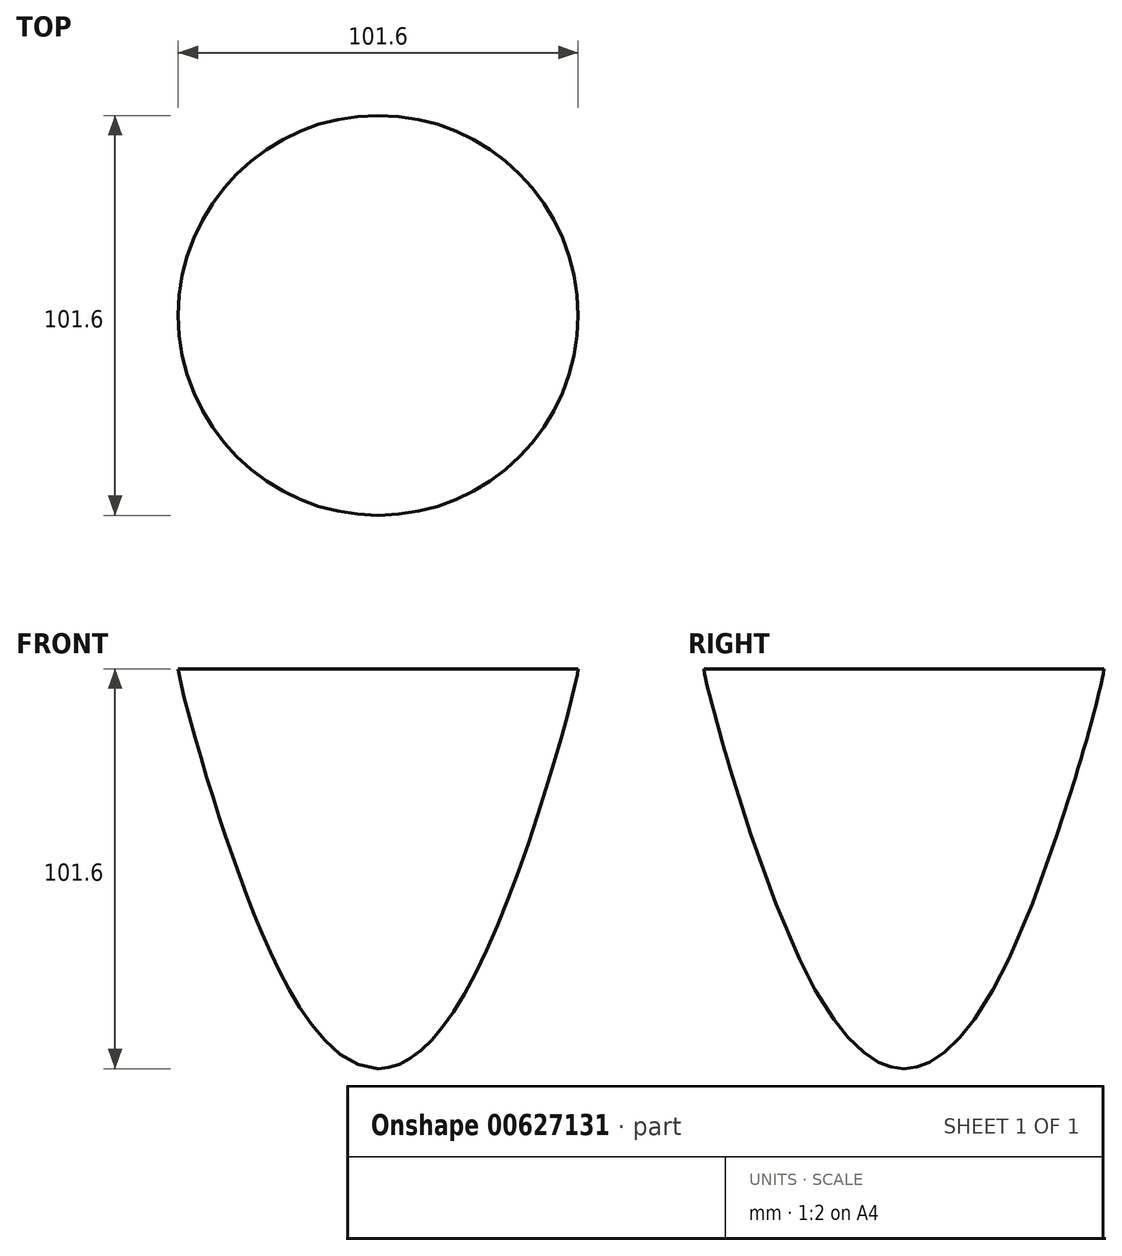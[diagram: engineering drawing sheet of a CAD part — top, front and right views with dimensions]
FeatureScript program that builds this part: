
annotation { "Feature Type Name" : "Feature", "Feature Type Description" : "" }
export const myFeature = defineFeature(function(context is Context, id is Id, definition is map)
    precondition{}
    {
        {
            var Q0;
            Q0=qCreatedBy(makeId("Front.planeOp"),FACE);
            var sketch = newSketch(context, id + "F0", { "sketchPlane" : qUnion([Q0])});
            skLineSegment(sketch, "E0", {"start": v(0, 0) * mm, "end": v(50.8, 0) * mm});
            skLineSegment(sketch, "E1", {"start": v(50.8, 0) * mm, "end": v(50.8, 101.6) * mm});
            skFitSpline(sketch, "E2", {"points": [v(0, 0) * mm, v(25.4, 25.4) * mm, v(50.8, 101.6) * mm], "startDerivative": vector(60.92, 0) * mm, "endDerivative": vector(0, 17.04) * mm});
            skPoint(sketch, "E3", {"position": v(25.4, 0) * mm});
            skPoint(sketch, "E4", {"position": v(50.8, 25.4) * mm});
            skLineSegment(sketch, "E5", {"start": v(25.4, 0) * mm, "end": v(25.4, 25.4) * mm});
            skLineSegment(sketch, "E6", {"start": v(50.8, 25.4) * mm, "end": v(25.4, 25.4) * mm});
            skLineSegment(sketch, "E7", {"start": v(0, 0) * mm, "end": v(0, 119.6) * mm});
            skPoint(sketch, "E8", {"position": v(12.7, 6.35) * mm});
            skPoint(sketch, "E9", {"position": v(12.7, 0) * mm});
            skPoint(sketch, "E10", {"position": v(0, 6.35) * mm});
            skLineSegment(sketch, "E11", {"start": v(0, 6.35) * mm, "end": v(12.7, 6.35) * mm});
            skLineSegment(sketch, "E12", {"start": v(12.7, 0) * mm, "end": v(12.7, 6.35) * mm});
            skPoint(sketch, "E13", {"position": v(38.1, 57.15) * mm});
            skPoint(sketch, "E14", {"position": v(50.8, 57.15) * mm});
            skPoint(sketch, "E15", {"position": v(38.1, 0) * mm});
            skLineSegment(sketch, "E16", {"start": v(38.1, 0) * mm, "end": v(38.1, 57.15) * mm});
            skLineSegment(sketch, "E17", {"start": v(50.8, 57.15) * mm, "end": v(38.1, 57.15) * mm});
            skLineSegment(sketch, "E18", {"start": v(50.8, 101.6) * mm, "end": v(0, 101.6) * mm});
            skSolve(sketch);
        }
        {
            var Q0;
            Q0=sQuery(id+"F0.wireOp",EDGE,"E2");
            var Q1;
            Q1=sQuery(id+"F0.wireOp",EDGE,"E18");
            var Q2;
            Q2=sQuery(id+"F0.wireOp",EDGE,"E7");
            revolve(context, id + "F1", {"bodyType" : ToolBodyType.SURFACE, "surfaceEntities" : qUnion([Q0, Q1]), "axis" : qUnion([Q2]), "revolveType" : RevolveType.FULL});
        }
    });
